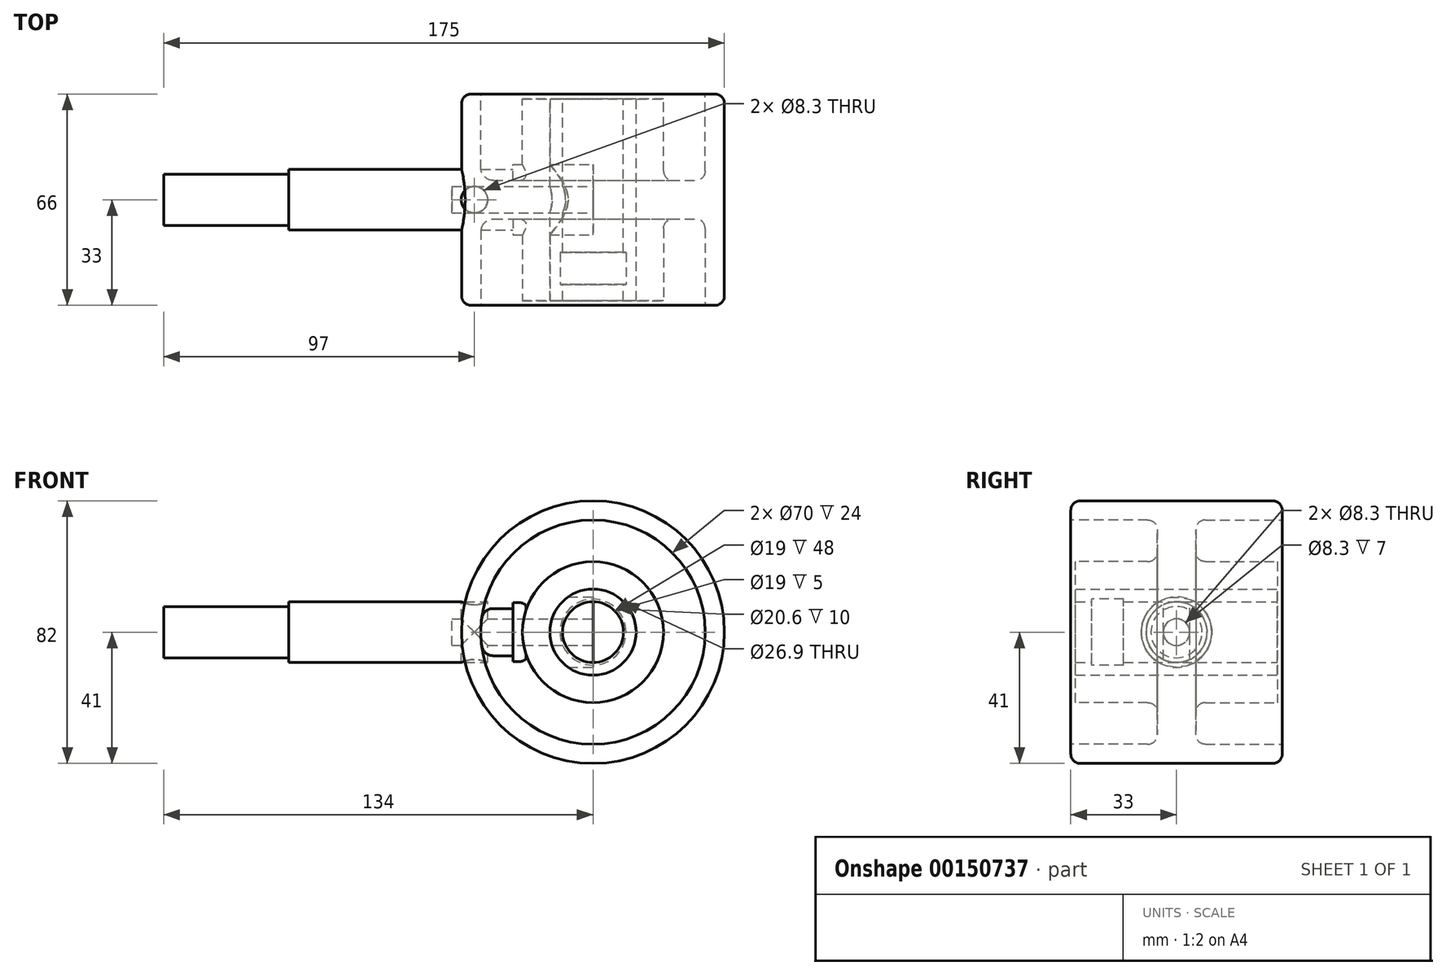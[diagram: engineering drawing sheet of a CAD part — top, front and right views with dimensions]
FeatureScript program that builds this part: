
annotation { "Feature Type Name" : "Feature", "Feature Type Description" : "" }
export const myFeature = defineFeature(function(context is Context, id is Id, definition is map)
    precondition{}
    {
        {
            var Q0;
            Q0=qCreatedBy(makeId("Front.planeOp"),FACE);
            var sketch = newSketch(context, id + "F0", { "sketchPlane" : qUnion([Q0])});
            skCircle(sketch, "E0", {"center": v(0, 0) * mm, "radius": 41 * mm});
            skCircle(sketch, "E1", {"center": v(0, 0) * mm, "radius": 35 * mm});
            skCircle(sketch, "E2", {"center": v(0, 0) * mm, "radius": 22 * mm});
            skCircle(sketch, "E3", {"center": v(0, 0) * mm, "radius": 13.45 * mm});
            skSolve(sketch);
        }
        {
            var Q0;
            Q0=makeQuery(id+"F0.imprint","IMPRINT",FACE,{"disambiguationData":[TD([[makeQuery(id+"F0.imprint","IMPRINT",EDGE,{"derivedFrom":sQuery(id+"F0.wireOp",EDGE,"E0")}),1.0]])]});
            var Q1;
            Q1=makeQuery(id+"F0.imprint","IMPRINT",FACE,{"disambiguationData":[TD([[makeQuery(id+"F0.imprint","IMPRINT",EDGE,{"derivedFrom":sQuery(id+"F0.wireOp",EDGE,"E1")}),1.0]])]});
            var Q2;
            Q2=makeQuery(id+"F0.imprint","IMPRINT",FACE,{"disambiguationData":[TD([[makeQuery(id+"F0.imprint","IMPRINT",EDGE,{"derivedFrom":sQuery(id+"F0.wireOp",EDGE,"E2")}),1.0]])]});
            var Q3;
            Q3=makeQuery(id+"F0.imprint","IMPRINT",FACE,{"disambiguationData":[TD([[makeQuery(id+"F0.imprint","IMPRINT",EDGE,{"derivedFrom":sQuery(id+"F0.wireOp",EDGE,"E3")}),1.0]])]});
            extrude(context, id + "F1", {"entities" : qUnion([Q0, Q1, Q2, Q3]), "endBound" : BoundingType.SYMMETRIC, "depth" : 66 * mm});
        }
        {
            var Q0;
            Q0=makeQuery(id+"F1.opExtrude","CAP_FACE",FACE,{"disambiguationData":[OSD([sQuery(id+"F0.wireOp",EDGE,"E0")])],"isStart":false});
            var sketch = newSketch(context, id + "F2", { "sketchPlane" : qUnion([Q0])});
            skCircle(sketch, "E4", {"center": v(0, 0) * mm, "radius": 35 * mm});
            skCircle(sketch, "E5", {"center": v(0, 0) * mm, "radius": 22 * mm});
            skSolve(sketch);
        }
        {
            var Q0;
            Q0=makeQuery(id+"F2.imprint","IMPRINT",FACE,{"disambiguationData":[TD([[makeQuery(id+"F2.imprint","IMPRINT",EDGE,{"derivedFrom":sQuery(id+"F2.wireOp",EDGE,"E4")}),1.0]])]});
            extrude(context, id + "F3", {"entities" : qUnion([Q0]), "operationType" : NewBodyOperationType.REMOVE, "oppositeDirection" : true, "depth" : 27 * mm});
        }
        {
            var Q0;
            Q0=makeQuery(id+"F1.opExtrude","CAP_FACE",FACE,{"disambiguationData":[OSD([sQuery(id+"F0.wireOp",EDGE,"E0")])],"isStart":true});
            var sketch = newSketch(context, id + "F4", { "sketchPlane" : qUnion([Q0])});
            skCircle(sketch, "E6", {"center": v(0, 0) * mm, "radius": 35 * mm});
            skCircle(sketch, "E7", {"center": v(0, 0) * mm, "radius": 22 * mm});
            skSolve(sketch);
        }
        {
            var Q0;
            Q0=makeQuery(id+"F4.imprint","IMPRINT",FACE,{"disambiguationData":[TD([[makeQuery(id+"F4.imprint","IMPRINT",EDGE,{"derivedFrom":sQuery(id+"F4.wireOp",EDGE,"E6")}),1.0]])]});
            extrude(context, id + "F5", {"entities" : qUnion([Q0]), "operationType" : NewBodyOperationType.REMOVE, "oppositeDirection" : true, "depth" : 27 * mm});
        }
        {
            var Q0;
            Q0=makeQuery(id+"F3.boolean.opBoolean","SPLIT",FACE,{"disambiguationData":[TD([makeQuery(id+"F3.opExtrude","SWEPT_FACE",FACE,{"disambiguationData":[OSD([sQuery(id+"F2.wireOp",EDGE,"E5")])]})])],"derivedFrom":makeQuery(id+"F1.opExtrude","CAP_FACE",FACE,{"disambiguationData":[OSD([sQuery(id+"F0.wireOp",EDGE,"E0")])],"isStart":false})});
            var sketch = newSketch(context, id + "F6", { "sketchPlane" : qUnion([Q0])});
            skCircle(sketch, "E8", {"center": v(0, 0) * mm, "radius": 13.45 * mm});
            skSolve(sketch);
        }
        {
            var Q0;
            Q0=makeQuery(id+"F6.imprint","IMPRINT",FACE,{"disambiguationData":[TD([[makeQuery(id+"F6.imprint","IMPRINT",EDGE,{"derivedFrom":sQuery(id+"F6.wireOp",EDGE,"E8")}),1.0]])]});
            extrude(context, id + "F7", {"entities" : qUnion([Q0]), "operationType" : NewBodyOperationType.REMOVE, "endBound" : BoundingType.THROUGH_ALL, "oppositeDirection" : true, "depth" : 25 * mm});
        }
        {
            var Q0;
            Q0=makeQuery(id+"F3.boolean.opBoolean","SPLIT",FACE,{"disambiguationData":[TD([makeQuery(id+"F3.opExtrude","SWEPT_FACE",FACE,{"disambiguationData":[OSD([sQuery(id+"F2.wireOp",EDGE,"E5")])]})])],"derivedFrom":makeQuery(id+"F1.opExtrude","CAP_FACE",FACE,{"disambiguationData":[OSD([sQuery(id+"F0.wireOp",EDGE,"E0")])],"isStart":false})});
            var sketch = newSketch(context, id + "F8", { "sketchPlane" : qUnion([Q0])});
            skCircle(sketch, "E9", {"center": v(0, 0) * mm, "radius": 13.45 * mm});
            skCircle(sketch, "E10", {"center": v(0, 0) * mm, "radius": 22 * mm});
            skSolve(sketch);
        }
        {
            var Q0;
            Q0=makeQuery(id+"F8.imprint","IMPRINT",FACE,{"disambiguationData":[TD([[makeQuery(id+"F8.imprint","IMPRINT",EDGE,{"derivedFrom":sQuery(id+"F8.wireOp",EDGE,"E9")}),-1.0]])]});
            extrude(context, id + "F9", {"entities" : qUnion([Q0]), "operationType" : NewBodyOperationType.REMOVE, "oppositeDirection" : true, "depth" : 1.5 * mm});
        }
        {
            var Q0;
            Q0=makeQuery(id+"F5.boolean.opBoolean","SPLIT",FACE,{"disambiguationData":[TD([makeQuery(id+"F5.opExtrude","SWEPT_FACE",FACE,{"disambiguationData":[OSD([sQuery(id+"F4.wireOp",EDGE,"E7")])]})])],"derivedFrom":makeQuery(id+"F1.opExtrude","CAP_FACE",FACE,{"disambiguationData":[OSD([sQuery(id+"F0.wireOp",EDGE,"E0")])],"isStart":true})});
            var sketch = newSketch(context, id + "F10", { "sketchPlane" : qUnion([Q0])});
            skCircle(sketch, "E11", {"center": v(0, 0) * mm, "radius": 13.45 * mm});
            skCircle(sketch, "E12", {"center": v(0, 0) * mm, "radius": 22 * mm});
            skSolve(sketch);
        }
        {
            var Q0;
            Q0=makeQuery(id+"F10.imprint","IMPRINT",FACE,{"disambiguationData":[TD([[makeQuery(id+"F10.imprint","IMPRINT",EDGE,{"derivedFrom":sQuery(id+"F10.wireOp",EDGE,"E11")}),1.0]])]});
            extrude(context, id + "F11", {"entities" : qUnion([Q0]), "operationType" : NewBodyOperationType.REMOVE, "oppositeDirection" : true, "depth" : 1.5 * mm});
        }
        {
            var Q0;
            Q0=makeQuery(id+"F1.opExtrude","CAP_EDGE",EDGE,{"disambiguationData":[OSD([sQuery(id+"F0.wireOp",EDGE,"E0")])],"isStart":true});
            var Q1;
            Q1=makeQuery(id+"F5.boolean.opBoolean","COPY",EDGE,{"derivedFrom":makeQuery(id+"F5.opExtrude","CAP_EDGE",EDGE,{"disambiguationData":[OSD([sQuery(id+"F4.wireOp",EDGE,"E6")])],"isStart":true})});
            var Q2;
            Q2=makeQuery(id+"F5.boolean.opBoolean","COPY",EDGE,{"derivedFrom":makeQuery(id+"F5.opExtrude","CAP_EDGE",EDGE,{"disambiguationData":[OSD([sQuery(id+"F4.wireOp",EDGE,"E6")])],"isStart":false})});
            var Q3;
            Q3=makeQuery(id+"F5.boolean.opBoolean","COPY",EDGE,{"derivedFrom":makeQuery(id+"F5.opExtrude","CAP_EDGE",EDGE,{"disambiguationData":[OSD([sQuery(id+"F4.wireOp",EDGE,"E7")])],"isStart":false})});
            var Q4;
            Q4=makeQuery(id+"F1.opExtrude","CAP_EDGE",EDGE,{"disambiguationData":[OSD([sQuery(id+"F0.wireOp",EDGE,"E0")])],"isStart":false});
            var Q5;
            Q5=makeQuery(id+"F3.boolean.opBoolean","COPY",EDGE,{"derivedFrom":makeQuery(id+"F3.opExtrude","CAP_EDGE",EDGE,{"disambiguationData":[OSD([sQuery(id+"F2.wireOp",EDGE,"E4")])],"isStart":true})});
            var Q6;
            Q6=makeQuery(id+"F3.boolean.opBoolean","COPY",EDGE,{"derivedFrom":makeQuery(id+"F3.opExtrude","CAP_EDGE",EDGE,{"disambiguationData":[OSD([sQuery(id+"F2.wireOp",EDGE,"E4")])],"isStart":false})});
            var Q7;
            Q7=makeQuery(id+"F3.boolean.opBoolean","COPY",EDGE,{"derivedFrom":makeQuery(id+"F3.opExtrude","CAP_EDGE",EDGE,{"disambiguationData":[OSD([sQuery(id+"F2.wireOp",EDGE,"E5")])],"isStart":false})});
            fillet(context, id + "F12", {"entities" : qUnion([Q0, Q1, Q2, Q3, Q4, Q5, Q6, Q7]), "radius" : 3 * mm, "tangentPropagation" : true, "allowEdgeOverflow" : false});
        }
        {
            var Q0;
            Q0=qCreatedBy(makeId("Front.planeOp"),FACE);
            var sketch = newSketch(context, id + "F13", { "sketchPlane" : qUnion([Q0])});
            skCircle(sketch, "E13", {"center": v(0, 0) * mm, "radius": 13.45 * mm});
            skCircle(sketch, "E14", {"center": v(0, 0) * mm, "radius": 9.5 * mm});
            skSolve(sketch);
        }
        {
            var Q0;
            Q0=makeQuery(id+"F13.imprint","IMPRINT",FACE,{"disambiguationData":[TD([[makeQuery(id+"F13.imprint","IMPRINT",EDGE,{"derivedFrom":sQuery(id+"F13.wireOp",EDGE,"E13")}),1.0]])]});
            extrude(context, id + "F14", {"entities" : qUnion([Q0]), "endBound" : BoundingType.SYMMETRIC, "depth" : 63 * mm});
        }
        {
            var Q0;
            Q0=qCreatedBy(makeId("Right.planeOp"),FACE);
            var sketch = newSketch(context, id + "F15", { "sketchPlane" : qUnion([Q0])});
            skLineSegment(sketch, "E15", {"start": v(31.5, 0) * mm, "end": v(-31.5, 0) * mm});
            skLineSegment(sketch, "E16", {"start": v(31.5, 0) * mm, "end": v(31.5, 9.5) * mm});
            skLineSegment(sketch, "E17", {"start": v(31.5, 9.5) * mm, "end": v(-16.5, 9.5) * mm});
            skLineSegment(sketch, "E18", {"start": v(-16.5, 9.5) * mm, "end": v(-16.5, 10.3) * mm});
            skLineSegment(sketch, "E19", {"start": v(-16.5, 10.3) * mm, "end": v(-26.5, 10.3) * mm});
            skLineSegment(sketch, "E20", {"start": v(-26.5, 10.3) * mm, "end": v(-26.5, 9.5) * mm});
            skLineSegment(sketch, "E21", {"start": v(-26.5, 9.5) * mm, "end": v(-31.5, 9.5) * mm});
            skLineSegment(sketch, "E22", {"start": v(-31.5, 9.5) * mm, "end": v(-31.5, 0) * mm});
            skPoint(sketch, "E23", {"position": v(-21.5, 10.3) * mm});
            skSolve(sketch);
        }
        {
            var Q0;
            Q0=makeQuery(id+"F15.imprint","IMPRINT",FACE,{"disambiguationData":[TD([[makeQuery(id+"F15.imprint","IMPRINT",EDGE,{"derivedFrom":sQuery(id+"F15.wireOp",EDGE,"E15")}),-1.0]])]});
            var Q1;
            Q1=sQuery(id+"F15.wireOp",EDGE,"E15");
            revolve(context, id + "F16", {"operationType" : NewBodyOperationType.REMOVE, "entities" : qUnion([Q0]), "axis" : qUnion([Q1]), "revolveType" : RevolveType.FULL, "oppositeDirection" : true});
        }
        {
            var Q0;
            Q0=qCreatedBy(makeId("Right.planeOp"),FACE);
            var sketch = newSketch(context, id + "F17", { "sketchPlane" : qUnion([Q0])});
            skCircle(sketch, "E24", {"center": v(0, 0) * mm, "radius": 11 * mm});
            skCircle(sketch, "E25", {"center": v(0, 0) * mm, "radius": 4.15 * mm});
            skSolve(sketch);
        }
        {
            var Q0;
            Q0=makeQuery(id+"F17.imprint","IMPRINT",FACE,{"disambiguationData":[TD([[makeQuery(id+"F17.imprint","IMPRINT",EDGE,{"derivedFrom":sQuery(id+"F17.wireOp",EDGE,"E24")}),1.0]])]});
            var Q1;
            Q1=makeQuery(id+"F17.imprint","IMPRINT",FACE,{"disambiguationData":[TD([[makeQuery(id+"F17.imprint","IMPRINT",EDGE,{"derivedFrom":sQuery(id+"F17.wireOp",EDGE,"E25")}),1.0]])]});
            extrude(context, id + "F18", {"entities" : qUnion([Q0, Q1]), "oppositeDirection" : true, "depth" : 25 * mm});
        }
        {
            var Q0;
            Q0=makeQuery(id+"F18.opExtrude","CAP_FACE",FACE,{"disambiguationData":[OSD([sQuery(id+"F17.wireOp",EDGE,"E24")])],"isStart":false});
            var sketch = newSketch(context, id + "F19", { "sketchPlane" : qUnion([Q0])});
            skCircle(sketch, "E26", {"center": v(0, 0) * mm, "radius": 9.5 * mm});
            skSolve(sketch);
        }
        {
            var Q0;
            Q0=makeQuery(id+"F19.imprint","IMPRINT",FACE,{"disambiguationData":[TD([[makeQuery(id+"F19.imprint","IMPRINT",EDGE,{"derivedFrom":sQuery(id+"F19.wireOp",EDGE,"E26")}),1.0]])]});
            extrude(context, id + "F20", {"entities" : qUnion([Q0]), "operationType" : NewBodyOperationType.ADD, "depth" : 70 * mm});
        }
        {
            var Q0;
            Q0=makeQuery(id+"F17.imprint","IMPRINT",FACE,{"disambiguationData":[TD([[makeQuery(id+"F17.imprint","IMPRINT",EDGE,{"derivedFrom":sQuery(id+"F17.wireOp",EDGE,"E25")}),1.0]])]});
            extrude(context, id + "F21", {"entities" : qUnion([Q0]), "operationType" : NewBodyOperationType.REMOVE, "oppositeDirection" : true, "depth" : 44 * mm});
        }
        {
            var Q0;
            Q0=qCreatedBy(makeId("Top.planeOp"),FACE);
            var sketch = newSketch(context, id + "F22", { "sketchPlane" : qUnion([Q0])});
            skCircle(sketch, "E27", {"center": v(-37, 0) * mm, "radius": 4.15 * mm});
            skSolve(sketch);
        }
        {
            var Q0;
            Q0=qSketchRegion(id+"F22",true);
            var Q1;
            Q1=makeQuery(id+"F20.opExtrude","SWEPT_FACE",FACE,{"disambiguationData":[OSD([sQuery(id+"F19.wireOp",EDGE,"E26")])]});
            var Q2;
            Q2=makeQuery(id+"F20.opExtrude","SWEPT_FACE",FACE,{"disambiguationData":[OSD([sQuery(id+"F19.wireOp",EDGE,"E26")])]});
            extrude(context, id + "F23", {"entities" : qUnion([Q0]), "operationType" : NewBodyOperationType.REMOVE, "endBound" : BoundingType.UP_TO_SURFACE, "oppositeDirection" : true, "endBoundEntityFace" : qUnion([Q1]), "depth" : 25 * mm, "hasSecondDirection" : true, "secondDirectionBound" : SecondDirectionBoundingType.UP_TO_SURFACE, "secondDirectionOppositeDirection" : false, "secondDirectionBoundEntityFace" : qUnion([Q2]), "secondDirectionDepth" : 25 * mm});
        }
        {
            var Q0;
            Q0=makeQuery(id+"F20.opExtrude","CAP_FACE",FACE,{"disambiguationData":[OSD([sQuery(id+"F19.wireOp",EDGE,"E26")])],"isStart":false});
            var sketch = newSketch(context, id + "F24", { "sketchPlane" : qUnion([Q0])});
            skCircle(sketch, "E28", {"center": v(0, 0) * mm, "radius": 8 * mm});
            skSolve(sketch);
        }
        {
            var Q0;
            Q0=makeQuery(id+"F24.imprint","IMPRINT",FACE,{"disambiguationData":[TD([[makeQuery(id+"F24.imprint","IMPRINT",EDGE,{"derivedFrom":sQuery(id+"F24.wireOp",EDGE,"E28")}),1.0]])]});
            extrude(context, id + "F25", {"entities" : qUnion([Q0]), "operationType" : NewBodyOperationType.ADD, "depth" : 39 * mm});
        }
    });
